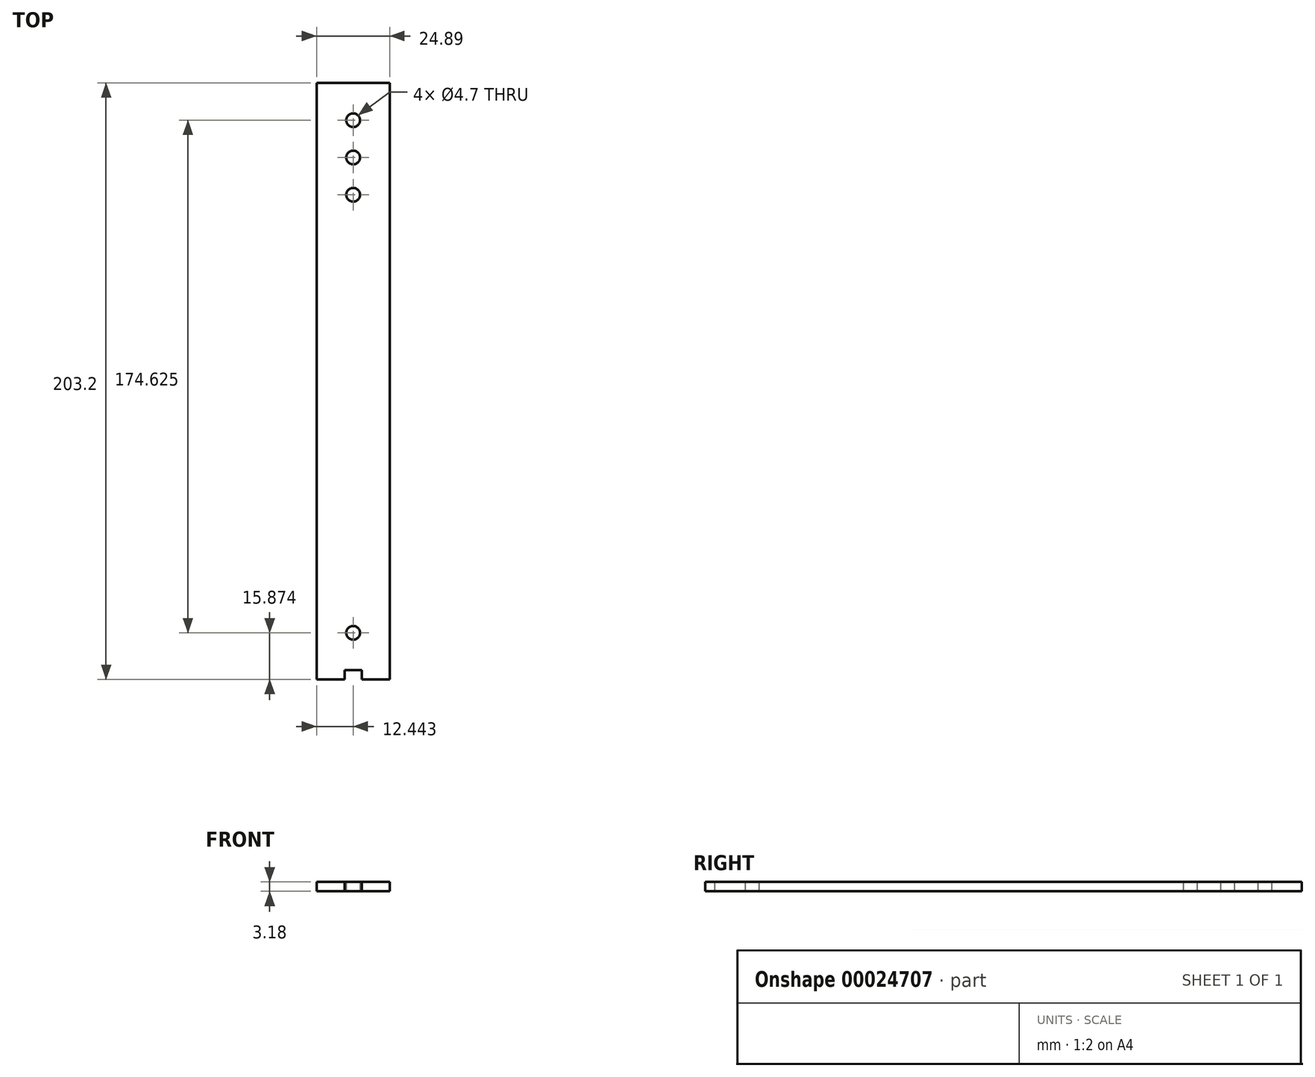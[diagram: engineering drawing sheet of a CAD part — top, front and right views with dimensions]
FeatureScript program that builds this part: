
annotation { "Feature Type Name" : "Feature", "Feature Type Description" : "" }
export const myFeature = defineFeature(function(context is Context, id is Id, definition is map)
    precondition{}
    {
        {
            var Q0;
            Q0=qCreatedBy(makeId("Top.planeOp"),FACE);
            var sketch = newSketch(context, id + "F0", { "sketchPlane" : qUnion([Q0])});
            skLineSegment(sketch, "E0", {"start": v(-104.81, -171.8) * mm, "end": v(-114.31, -171.8) * mm});
            skLineSegment(sketch, "E1.top", {"start": v(-129.7, 31.4) * mm, "end": v(-104.81, 31.4) * mm});
            skLineSegment(sketch, "E1.left", {"start": v(-129.7, -171.8) * mm, "end": v(-129.7, 31.4) * mm});
            skLineSegment(sketch, "E1.right", {"start": v(-104.81, -171.8) * mm, "end": v(-104.81, 31.4) * mm});
            skLineSegment(sketch, "E2", {"start": v(-129.7, -171.8) * mm, "end": v(-120.2, -171.8) * mm});
            skCircle(sketch, "E3", {"center": v(-117.26, 18.7) * mm, "radius": 2.35 * mm});
            skCircle(sketch, "E4", {"center": v(-117.26, 6) * mm, "radius": 2.35 * mm});
            skCircle(sketch, "E5", {"center": v(-117.26, -6.7) * mm, "radius": 2.35 * mm});
            skCircle(sketch, "E6", {"center": v(-117.26, -155.93) * mm, "radius": 2.35 * mm});
            skLineSegment(sketch, "E7.top", {"start": v(-120.2, -168.63) * mm, "end": v(-114.31, -168.63) * mm});
            skLineSegment(sketch, "E7.right", {"start": v(-114.31, -171.8) * mm, "end": v(-114.31, -168.63) * mm});
            skLineSegment(sketch, "E7.left", {"start": v(-120.2, -171.8) * mm, "end": v(-120.2, -168.63) * mm});
            skSolve(sketch);
        }
        {
            var Q0;
            Q0=makeQuery(id+"F0.imprint","IMPRINT",FACE,{"disambiguationData":[TD([[makeQuery(id+"F0.imprint","IMPRINT",EDGE,{"derivedFrom":sQuery(id+"F0.wireOp",EDGE,"E0")}),-1.0]])]});
            extrude(context, id + "F1", {"entities" : qUnion([Q0]), "depth" : 3.17 * mm});
        }
    });
